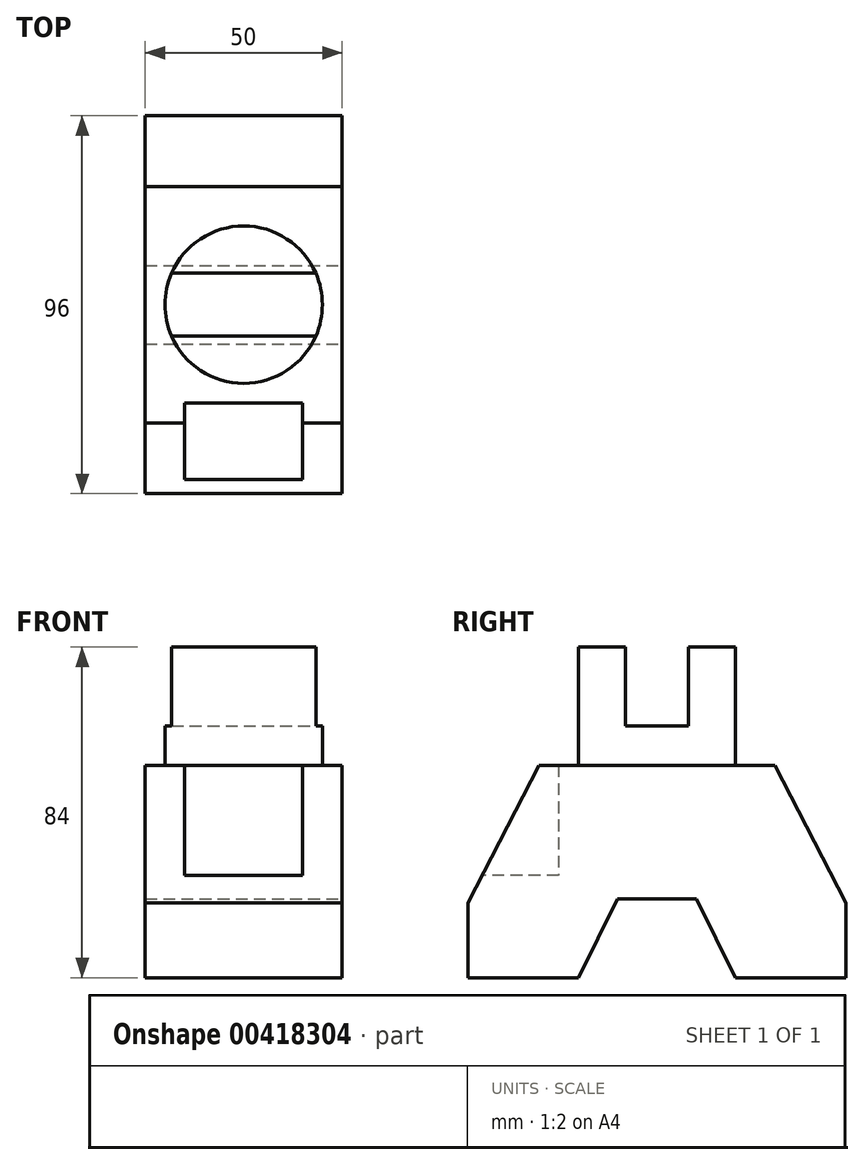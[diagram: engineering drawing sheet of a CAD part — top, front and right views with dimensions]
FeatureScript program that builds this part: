
annotation { "Feature Type Name" : "Feature", "Feature Type Description" : "" }
export const myFeature = defineFeature(function(context is Context, id is Id, definition is map)
    precondition{}
    {
        {
            var Q0;
            Q0=qCreatedBy(makeId("Right.planeOp"),FACE);
            var sketch = newSketch(context, id + "F0", { "sketchPlane" : qUnion([Q0])});
            skLineSegment(sketch, "E0.bottom", {"start": v(-48, 27) * mm, "end": v(48, 27) * mm});
            skLineSegment(sketch, "E0.top", {"start": v(-48, -27) * mm, "end": v(48, -27) * mm});
            skLineSegment(sketch, "E0.left", {"start": v(-48, 27) * mm, "end": v(-48, -27) * mm});
            skLineSegment(sketch, "E0.right", {"start": v(48, 27) * mm, "end": v(48, -27) * mm});
            skPoint(sketch, "E0.middle", {"position": v(0, 0) * mm});
            skSolve(sketch);
        }
        {
            var Q0;
            Q0 = qSketchRegion(id + "F0", true);
            extrude(context, id + "F1", {"entities" : qUnion([Q0]), "endBound" : BoundingType.SYMMETRIC, "depth" : 50 * mm});
        }
        {
            var Q0;
            Q0=makeQuery(id+"F1.opExtrude","SWEPT_EDGE",EDGE,{"disambiguationData":[OSD([sQuery(id+"F0.wireOp",EDGE,"E0.bottom"),sQuery(id+"F0.wireOp",EDGE,"E0.left")])]});
            var Q1;
            Q1=makeQuery(id+"F1.opExtrude","SWEPT_EDGE",EDGE,{"disambiguationData":[OSD([sQuery(id+"F0.wireOp",EDGE,"E0.bottom"),sQuery(id+"F0.wireOp",EDGE,"E0.right")])]});
            chamfer(context, id + "F2", {"entities" : qUnion([Q0, Q1]), "chamferType" : ChamferType.TWO_OFFSETS, "width1" : ((96 - 60) / 2) * mm, "oppositeDirection" : true, "width2" : (50 - 15) * mm});
        }
        {
            var Q0;
            Q0=makeQuery(id+"F1.opExtrude","CAP_FACE",FACE,{"disambiguationData":[OSD([sQuery(id+"F0.wireOp",EDGE,"E0.bottom"),sQuery(id+"F0.wireOp",EDGE,"E0.top"),sQuery(id+"F0.wireOp",EDGE,"E0.left"),sQuery(id+"F0.wireOp",EDGE,"E0.right")])],"isStart":false});
            var sketch = newSketch(context, id + "F3", { "sketchPlane" : qUnion([Q0])});
            skLineSegment(sketch, "E1", {"start": v(-20, -27) * mm, "end": v(-10, -7) * mm});
            skLineSegment(sketch, "E2", {"start": v(-10, -7) * mm, "end": v(10, -7) * mm});
            skLineSegment(sketch, "E3", {"start": v(-20, -27) * mm, "end": v(20, -27) * mm});
            skLineSegment(sketch, "E4", {"start": v(10, -7) * mm, "end": v(20, -27) * mm});
            skLineSegment(sketch, "E5", {"start": v(0, -7) * mm, "end": v(0, -21.37) * mm, "construction": true});
            skSolve(sketch);
        }
        {
            var Q0;
            Q0 = qSketchRegion(id + "F3", true);
            extrude(context, id + "F4", {"entities" : qUnion([Q0]), "operationType" : NewBodyOperationType.REMOVE, "endBound" : BoundingType.THROUGH_ALL, "oppositeDirection" : true, "depth" : 25 * mm});
        }
        {
            var Q0;
            Q0=makeQuery(id+"F1.opExtrude","SWEPT_FACE",FACE,{"disambiguationData":[OSD([sQuery(id+"F0.wireOp",EDGE,"E0.bottom")])]});
            var sketch = newSketch(context, id + "F5", { "sketchPlane" : qUnion([Q0])});
            skCircle(sketch, "E6", {"center": v(0, 0) * mm, "radius": 20 * mm});
            skSolve(sketch);
        }
        {
            var Q0;
            Q0 = qSketchRegion(id + "F5", true);
            extrude(context, id + "F6", {"entities" : qUnion([Q0]), "operationType" : NewBodyOperationType.ADD, "depth" : 30 * mm});
        }
        {
            var Q0;
            Q0=makeQuery(id+"F6.opExtrude","CAP_FACE",FACE,{"disambiguationData":[OSD([sQuery(id+"F5.wireOp",EDGE,"E6")])],"isStart":false});
            var sketch = newSketch(context, id + "F7", { "sketchPlane" : qUnion([Q0])});
            skLineSegment(sketch, "E7.bottom", {"start": v(-20, 8) * mm, "end": v(20, 8) * mm});
            skLineSegment(sketch, "E7.top", {"start": v(-20, -8) * mm, "end": v(20, -8) * mm});
            skLineSegment(sketch, "E7.left", {"start": v(-20, 8) * mm, "end": v(-20, -8) * mm});
            skLineSegment(sketch, "E7.right", {"start": v(20, 8) * mm, "end": v(20, -8) * mm});
            skPoint(sketch, "E7.middle", {"position": v(0, 0) * mm});
            skSolve(sketch);
        }
        {
            var Q0;
            Q0 = qSketchRegion(id + "F7", true);
            extrude(context, id + "F8", {"entities" : qUnion([Q0]), "operationType" : NewBodyOperationType.REMOVE, "oppositeDirection" : true, "depth" : 20 * mm});
        }
        {
            var Q0;
            Q0=makeQuery(id+"F1.opExtrude","SWEPT_FACE",FACE,{"disambiguationData":[OSD([sQuery(id+"F0.wireOp",EDGE,"E0.left")])]});
            var sketch = newSketch(context, id + "F9", { "sketchPlane" : qUnion([Q0])});
            skLineSegment(sketch, "E8.bottom", {"start": v(-15, 27) * mm, "end": v(15, 27) * mm});
            skLineSegment(sketch, "E8.top", {"start": v(-15, -1) * mm, "end": v(15, -1) * mm});
            skLineSegment(sketch, "E8.left", {"start": v(-15, 27) * mm, "end": v(-15, -1) * mm});
            skLineSegment(sketch, "E8.right", {"start": v(15, 27) * mm, "end": v(15, -1) * mm});
            skSolve(sketch);
        }
        {
            var Q0;
            Q0 = qSketchRegion(id + "F9", true);
            extrude(context, id + "F10", {"entities" : qUnion([Q0]), "operationType" : NewBodyOperationType.REMOVE, "oppositeDirection" : true, "depth" : (96 / 2 - 25) * mm});
        }
    });
